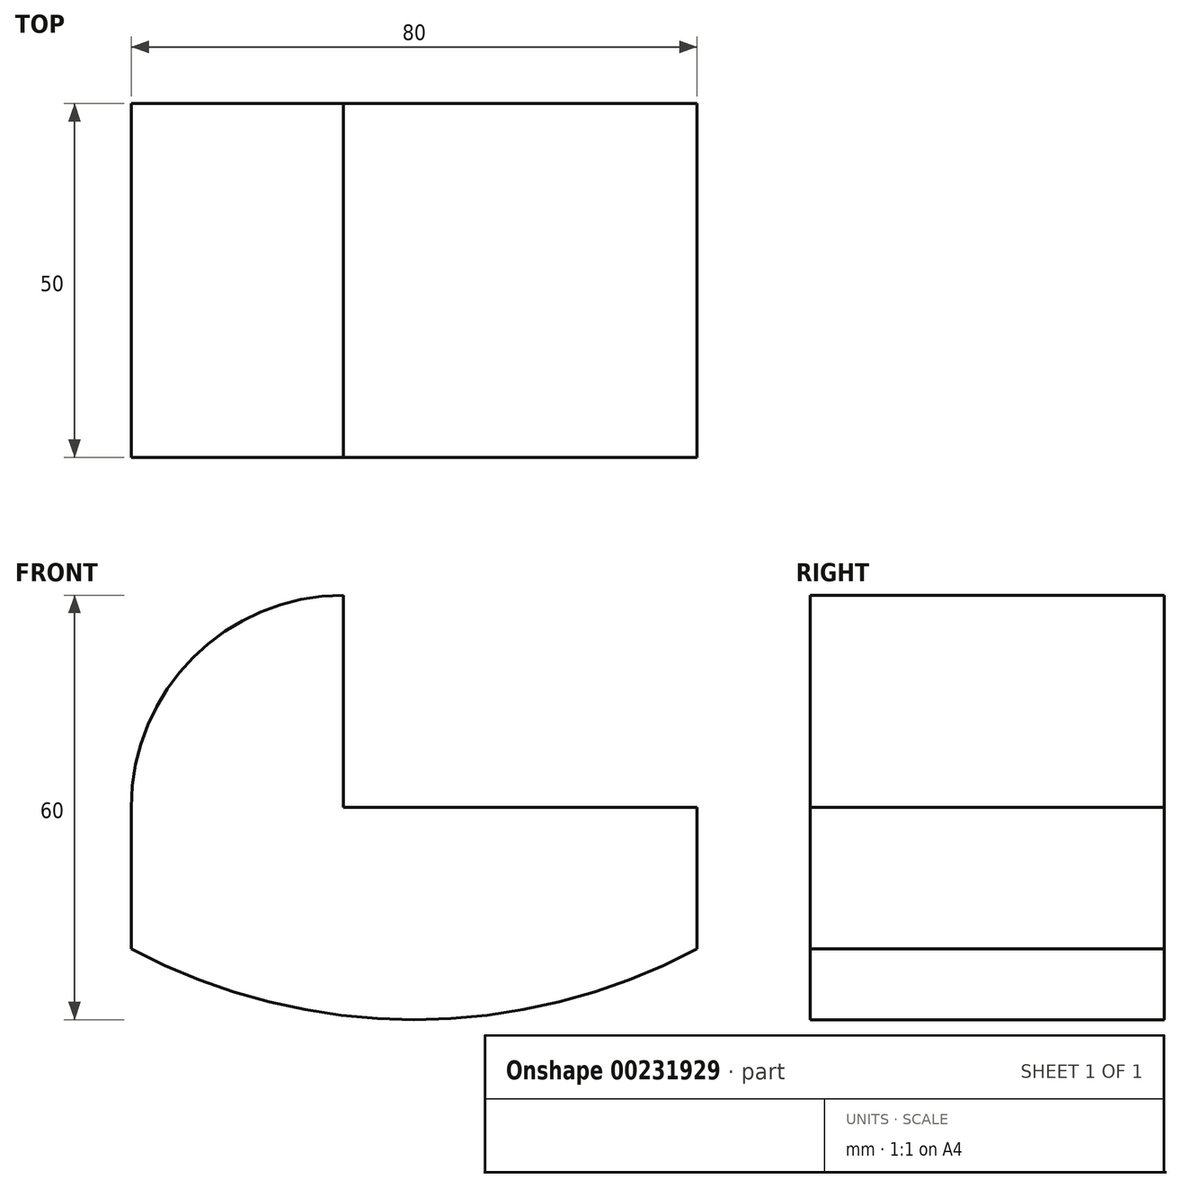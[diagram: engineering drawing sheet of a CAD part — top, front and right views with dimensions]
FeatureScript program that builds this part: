
annotation { "Feature Type Name" : "Feature", "Feature Type Description" : "" }
export const myFeature = defineFeature(function(context is Context, id is Id, definition is map)
    precondition{}
    {
        {
            var Q0;
            Q0=qCreatedBy(makeId("Front.planeOp"),FACE);
            var sketch = newSketch(context, id + "F0", { "sketchPlane" : qUnion([Q0])});
            skLineSegment(sketch, "E0", {"start": v(0, 0) * mm, "end": v(50, 0) * mm});
            skLineSegment(sketch, "E1", {"start": v(0, 0) * mm, "end": v(0, 30) * mm});
            skArc(sketch, "E2", {"start": v(0, 30) * mm, "mid": v(-21.21, 21.21) * mm, "end": v(-30, 0) * mm});
            skLineSegment(sketch, "E3", {"start": v(-30, 0) * mm, "end": v(-30, -20) * mm});
            skLineSegment(sketch, "E4", {"start": v(50, 0) * mm, "end": v(50, -20) * mm});
            skArc(sketch, "E5", {"start": v(-30, -20) * mm, "mid": v(10, -30) * mm, "end": v(50, -20) * mm});
            skSolve(sketch);
        }
        {
            var Q0;
            Q0=makeQuery(id+"F0.imprint","IMPRINT",FACE,{"disambiguationData":[TD([[makeQuery(id+"F0.imprint","IMPRINT",EDGE,{"derivedFrom":sQuery(id+"F0.wireOp",EDGE,"E0")}),-1.0]])]});
            extrude(context, id + "F1", {"entities" : qUnion([Q0]), "endBound" : BoundingType.SYMMETRIC, "depth" : 50 * mm});
        }
    });
